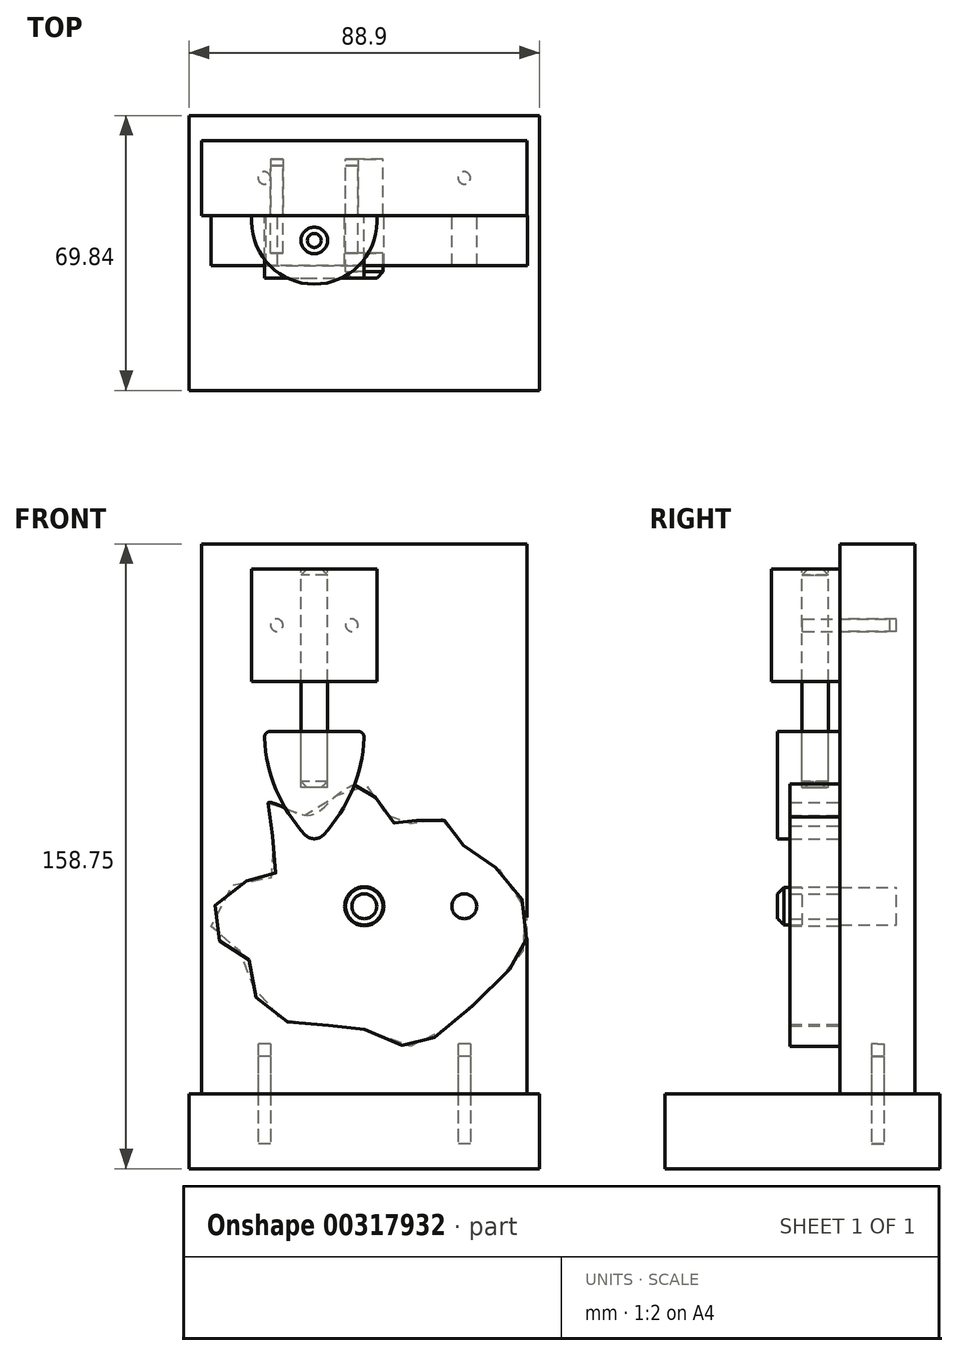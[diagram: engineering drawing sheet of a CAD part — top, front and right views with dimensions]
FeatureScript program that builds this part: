
annotation { "Feature Type Name" : "Feature", "Feature Type Description" : "" }
export const myFeature = defineFeature(function(context is Context, id is Id, definition is map)
    precondition{}
    {
        {
            var Q0;
            Q0=qCreatedBy(makeId("Top.planeOp"),FACE);
            var sketch = newSketch(context, id + "F0", { "sketchPlane" : qUnion([Q0])});
            skLineSegment(sketch, "E0.bottom", {"start": v(44.45, 34.93) * mm, "end": v(-44.45, 34.93) * mm});
            skLineSegment(sketch, "E0.top", {"start": v(44.45, -34.93) * mm, "end": v(-44.45, -34.93) * mm});
            skLineSegment(sketch, "E0.left", {"start": v(44.45, 34.92) * mm, "end": v(44.45, -34.93) * mm});
            skLineSegment(sketch, "E0.right", {"start": v(-44.45, 34.93) * mm, "end": v(-44.45, -34.93) * mm});
            skPoint(sketch, "E0.middle", {"position": v(0, 0) * mm});
            skSolve(sketch);
        }
        {
            var Q0;
            Q0=qCreatedBy(makeId("Front.planeOp"),FACE);
            cPlane(context, id + "F1", {"entities" : qUnion([Q0]), "cplaneType" : CPlaneType.OFFSET, "offset" : 28.57 * mm, "oppositeDirection" : true, "width" : 152.4 * mm, "height" : 152.4 * mm});
        }
        {
            var Q0;
            Q0=qCreatedBy(id+"F1.planeOp",FACE);
            var sketch = newSketch(context, id + "F2", { "sketchPlane" : qUnion([Q0])});
            skLineSegment(sketch, "E1.bottom", {"start": v(41.28, 0) * mm, "end": v(-41.28, 0) * mm});
            skLineSegment(sketch, "E1.top", {"start": v(41.27, 139.7) * mm, "end": v(-41.27, 139.7) * mm});
            skLineSegment(sketch, "E1.left", {"start": v(41.28, 0) * mm, "end": v(41.28, 139.7) * mm});
            skLineSegment(sketch, "E1.right", {"start": v(-41.28, 0) * mm, "end": v(-41.27, 139.7) * mm});
            skLineSegment(sketch, "E2", {"start": v(0, 0) * mm, "end": v(0, 139.7) * mm, "construction": true});
            skSolve(sketch);
        }
        {
            var Q0;
            Q0=makeQuery(id+"F0.imprint","IMPRINT",FACE,{"disambiguationData":[TD([[makeQuery(id+"F0.imprint","IMPRINT",EDGE,{"derivedFrom":sQuery(id+"F0.wireOp",EDGE,"E0.bottom")}),1.0]])]});
            extrude(context, id + "F3", {"entities" : qUnion([Q0]), "oppositeDirection" : true, "depth" : 19.05 * mm});
        }
        {
            var Q0;
            Q0=makeQuery(id+"F2.imprint","IMPRINT",FACE,{"disambiguationData":[TD([[makeQuery(id+"F2.imprint","IMPRINT",EDGE,{"derivedFrom":sQuery(id+"F2.wireOp",EDGE,"E1.bottom")}),-1.0]])]});
            extrude(context, id + "F4", {"entities" : qUnion([Q0]), "depth" : 19.05 * mm});
        }
        {
            var Q0;
            Q0=qCreatedBy(makeId("Top.planeOp"),FACE);
            var sketch = newSketch(context, id + "F5", { "sketchPlane" : qUnion([Q0])});
            skPoint(sketch, "E3.0", {"position": v(-41.27, 19.05) * mm});
            skPoint(sketch, "E4.0", {"position": v(41.28, 19.05) * mm});
            skLineSegment(sketch, "E5", {"start": v(-41.27, 19.05) * mm, "end": v(41.28, 19.05) * mm, "construction": true});
            skPoint(sketch, "E6.0", {"position": v(0, 9.53) * mm});
            skPoint(sketch, "E7.0", {"position": v(0, 28.58) * mm});
            skLineSegment(sketch, "E8", {"start": v(0, 28.58) * mm, "end": v(0, 9.53) * mm, "construction": true});
            skPoint(sketch, "E9", {"position": v(-25.4, 19.05) * mm});
            skPoint(sketch, "E10", {"position": v(25.4, 19.05) * mm});
            skCircle(sketch, "E11", {"center": v(-25.4, 19.05) * mm, "radius": 1.59 * mm});
            skCircle(sketch, "E12", {"center": v(25.4, 19.05) * mm, "radius": 1.59 * mm});
            skSolve(sketch);
        }
        {
            var Q0;
            Q0 = qSketchRegion(id + "F5", true);
            var Q1;
            Q1=sQuery(id+"F5.wireOp",EDGE,"E11");
            var Q2;
            Q2=sQuery(id+"F5.wireOp",EDGE,"E12");
            extrude(context, id + "F6", {"entities" : qUnion([Q0]), "operationType" : NewBodyOperationType.REMOVE, "surfaceEntities" : qUnion([Q1, Q2]), "endBound" : BoundingType.SYMMETRIC, "depth" : 25.4 * mm});
        }
        {
            var Q0;
            Q0 = qSketchRegion(id + "F5", true);
            extrude(context, id + "F7", {"entities" : qUnion([Q0]), "depth" : 9.52 * mm, "hasSecondDirection" : true, "secondDirectionOppositeDirection" : true, "secondDirectionDepth" : 12.7 * mm});
        }
        {
            var Q0;
            Q0=makeQuery(id+"F4.opExtrude","CAP_FACE",FACE,{"disambiguationData":[OSD([sQuery(id+"F2.wireOp",EDGE,"E1.bottom"),sQuery(id+"F2.wireOp",EDGE,"E1.top"),sQuery(id+"F2.wireOp",EDGE,"E1.left"),sQuery(id+"F2.wireOp",EDGE,"E1.right")])],"isStart":false});
            var sketch = newSketch(context, id + "F8", { "sketchPlane" : qUnion([Q0])});
            skPoint(sketch, "E13", {"position": v(0, 47.63) * mm});
            skCircle(sketch, "E14", {"center": v(0, 47.63) * mm, "radius": 4.76 * mm});
            skCircle(sketch, "E15", {"center": v(-22.22, 119.03) * mm, "radius": 1.59 * mm});
            skLineSegment(sketch, "E16", {"start": v(-22.22, 119.03) * mm, "end": v(-3.17, 119.03) * mm, "construction": true});
            skCircle(sketch, "E17", {"center": v(-3.17, 119.03) * mm, "radius": 1.59 * mm});
            skSolve(sketch);
        }
        {
            var Q0;
            Q0 = qSketchRegion(id + "F8", true);
            extrude(context, id + "F9", {"entities" : qUnion([Q0]), "operationType" : NewBodyOperationType.REMOVE, "oppositeDirection" : true, "depth" : 14.29 * mm});
        }
        {
            var Q0;
            Q0=makeQuery(id+"F8.imprint","IMPRINT",FACE,{"disambiguationData":[TD([[makeQuery(id+"F8.imprint","IMPRINT",EDGE,{"derivedFrom":sQuery(id+"F8.wireOp",EDGE,"E14")}),1.0]])]});
            extrude(context, id + "F10", {"entities" : qUnion([Q0]), "depth" : 15.88 * mm, "hasSecondDirection" : true, "secondDirectionOppositeDirection" : true, "secondDirectionDepth" : 14.29 * mm});
        }
        {
            var Q0;
            Q0=makeQuery(id+"F10.opExtrude","CAP_EDGE",EDGE,{"disambiguationData":[OSD([sQuery(id+"F8.wireOp",EDGE,"E14")])],"isStart":false});
            chamfer(context, id + "F11", {"entities" : qUnion([Q0]), "width" : 1.59 * mm, "tangentPropagation" : true});
        }
        {
            var Q0;
            Q0=makeQuery(id+"F4.opExtrude","SWEPT_FACE",FACE,{"disambiguationData":[OSD([sQuery(id+"F2.wireOp",EDGE,"E1.top")])]});
            cPlane(context, id + "F12", {"entities" : qUnion([Q0]), "cplaneType" : CPlaneType.OFFSET, "offset" : 6.35 * mm, "oppositeDirection" : true, "width" : 152.4 * mm, "height" : 152.4 * mm});
        }
        {
            var Q0;
            Q0=qCreatedBy(id+"F12.planeOp",FACE);
            var sketch = newSketch(context, id + "F13", { "sketchPlane" : qUnion([Q0])});
            skPoint(sketch, "E18.0", {"position": v(-12.7, 9.53) * mm});
            skPoint(sketch, "E19", {"position": v(-12.7, 7.94) * mm});
            skCircle(sketch, "E20", {"center": v(-12.7, 3.18) * mm, "radius": 3.37 * mm});
            skLineSegment(sketch, "E21", {"start": v(-12.7, 9.53) * mm, "end": v(-12.7, 3.18) * mm, "construction": true});
            skArc(sketch, "E22", {"start": v(-28.57, 7.94) * mm, "mid": v(-12.7, -7.94) * mm, "end": v(3.18, 7.94) * mm});
            skLineSegment(sketch, "E23", {"start": v(-28.57, 7.94) * mm, "end": v(-28.57, 9.53) * mm});
            skLineSegment(sketch, "E24", {"start": v(-28.57, 9.53) * mm, "end": v(3.18, 9.53) * mm});
            skLineSegment(sketch, "E25", {"start": v(3.18, 9.53) * mm, "end": v(3.18, 7.94) * mm});
            skSolve(sketch);
        }
        {
            var Q0;
            Q0=makeQuery(id+"F13.imprint","IMPRINT",FACE,{"disambiguationData":[TD([[makeQuery(id+"F13.imprint","IMPRINT",EDGE,{"derivedFrom":sQuery(id+"F13.wireOp",EDGE,"E20")}),-1.0]])]});
            extrude(context, id + "F14", {"entities" : qUnion([Q0]), "oppositeDirection" : true, "depth" : 28.57 * mm});
        }
        {
            var Q0;
            Q0=sQuery(id+"F8.wireOp",EDGE,"E17");
            var Q1;
            Q1=sQuery(id+"F8.wireOp",EDGE,"E15");
            extrude(context, id + "F15", {"bodyType" : ToolBodyType.SURFACE, "surfaceEntities" : qUnion([Q0, Q1]), "depth" : 1.59 * mm});
        }
        {
            var Q0;
            Q0=makeQuery(id+"F13.imprint","IMPRINT",FACE,{"disambiguationData":[TD([[makeQuery(id+"F13.imprint","IMPRINT",EDGE,{"derivedFrom":sQuery(id+"F13.wireOp",EDGE,"E20")}),1.0]])]});
            extrude(context, id + "F16", {"entities" : qUnion([Q0]), "oppositeDirection" : true, "depth" : 55.56 * mm});
        }
        {
            var Q0;
            Q0=makeQuery(id+"F8.imprint","IMPRINT",FACE,{"disambiguationData":[TD([[makeQuery(id+"F8.imprint","IMPRINT",EDGE,{"derivedFrom":sQuery(id+"F8.wireOp",EDGE,"E14")}),-1.0]])]});
            var sketch = newSketch(context, id + "F17", { "sketchPlane" : qUnion([Q0])});
            skLineSegment(sketch, "E26", {"start": v(-23.78, 92.08) * mm, "end": v(-1.62, 92.08) * mm});
            skLineSegment(sketch, "E27", {"start": v(-12.7, 92.08) * mm, "end": v(-12.7, 63.5) * mm, "construction": true});
            skArc(sketch, "E28", {"start": v(-10.38, 65.78) * mm, "mid": v(-3, 77.17) * mm, "end": v(-0.04, 90.42) * mm});
            skArc(sketch, "E29.MirrorCS", {"start": v(-15.02, 65.78) * mm, "mid": v(-22.4, 77.17) * mm, "end": v(-25.36, 90.42) * mm});
            skPoint(sketch, "E30.visualSharp", {"position": v(-25.4, 92.08) * mm});
            skArc(sketch, "E30.filletArc", {"start": v(-23.78, 92.08) * mm, "mid": v(-24.92, 91.59) * mm, "end": v(-25.36, 90.42) * mm});
            skPoint(sketch, "E31.visualSharp", {"position": v(0, 92.08) * mm});
            skArc(sketch, "E31.filletArc", {"start": v(-0.04, 90.42) * mm, "mid": v(-0.48, 91.59) * mm, "end": v(-1.62, 92.08) * mm});
            skPoint(sketch, "E32.visualSharp", {"position": v(-12.7, 63.5) * mm});
            skArc(sketch, "E32.filletArc", {"start": v(-15.02, 65.78) * mm, "mid": v(-12.7, 64.77) * mm, "end": v(-10.38, 65.78) * mm});
            skSolve(sketch);
        }
        {
            var Q0;
            Q0 = qSketchRegion(id + "F17", true);
            extrude(context, id + "F18", {"entities" : qUnion([Q0]), "depth" : 15.88 * mm});
        }
        {
            var Q0;
            Q0=makeQuery(id+"F18.opExtrude","SWEPT_BODY",BODY,{"disambiguationData":[OSD([sQuery(id+"F17.wireOp",EDGE,"E26"),sQuery(id+"F17.wireOp",EDGE,"E28"),sQuery(id+"F17.wireOp",EDGE,"E29.MirrorCS"),sQuery(id+"F17.wireOp",EDGE,"E30.filletArc"),sQuery(id+"F17.wireOp",EDGE,"E31.filletArc"),sQuery(id+"F17.wireOp",EDGE,"E32.filletArc")])]});
            var Q1;
            Q1=makeQuery(id+"F16.opExtrude","SWEPT_BODY",BODY,{"disambiguationData":[OSD([sQuery(id+"F13.wireOp",EDGE,"E20")])]});
            booleanBodies(context, id + "F19", {"operationType" : BooleanOperationType.INTERSECTION, "tools" : qUnion([Q0, Q1]), "keepTools" : true});
        }
        {
            var Q0;
            Q0=makeQuery(id+"F16.opExtrude","CAP_EDGE",EDGE,{"disambiguationData":[OSD([sQuery(id+"F13.wireOp",EDGE,"E20")])],"isStart":false});
            var Q1;
            Q1=makeQuery(id+"F16.opExtrude","CAP_EDGE",EDGE,{"disambiguationData":[OSD([sQuery(id+"F13.wireOp",EDGE,"E20")])],"isStart":true});
            chamfer(context, id + "F20", {"entities" : qUnion([Q0, Q1]), "width" : 1.59 * mm, "tangentPropagation" : true});
        }
        {
            var Q0;
            Q0=makeQuery(id+"F8.imprint","IMPRINT",FACE,{"disambiguationData":[TD([[makeQuery(id+"F8.imprint","IMPRINT",EDGE,{"derivedFrom":sQuery(id+"F8.wireOp",EDGE,"E14")}),-1.0]])]});
            var sketch = newSketch(context, id + "F21", { "sketchPlane" : qUnion([Q0])});
            skPoint(sketch, "E33.0", {"position": v(0, 47.63) * mm});
            skCircle(sketch, "E34", {"center": v(0, 47.63) * mm, "radius": 4.96 * mm});
            skCircle(sketch, "E35", {"center": v(25.4, 47.63) * mm, "radius": 3.18 * mm});
            skLineSegment(sketch, "E36", {"start": v(0, 47.63) * mm, "end": v(25.4, 47.63) * mm, "construction": true});
            skFitSpline(sketch, "E37", {"points": [v(-24.47, 73.9) * mm, v(-14.78, 70.74) * mm, v(-7.03, 75.83) * mm, v(0, 78.5) * mm, v(4.36, 72.68) * mm, v(9.2, 68.08) * mm, v(14.05, 69.77) * mm, v(20.6, 69.29) * mm, v(25.92, 62.26) * mm, v(37.07, 54.51) * mm, v(41.43, 40.7) * mm, v(36.83, 31.5) * mm, v(20.1, 15.99) * mm, v(10.42, 12.11) * mm, v(-2.42, 17.2) * mm, v(-13.8, 17.2) * mm, v(-26.9, 23.26) * mm, v(-29.8, 34.64) * mm, v(-38.28, 40.46) * mm, v(-33.92, 52.81) * mm, v(-23.5, 55) * mm, v(-22.77, 63.23) * mm, v(-24.47, 73.9) * mm]});
            skSolve(sketch);
        }
        {
            var Q0;
            Q0 = qSketchRegion(id + "F21", true);
            extrude(context, id + "F22", {"entities" : qUnion([Q0]), "depth" : 12.7 * mm});
        }
        {
            var Q0;
            Q0 = qSketchRegion(id + "F8", true);
            extrude(context, id + "F23", {"entities" : qUnion([Q0]), "operationType" : NewBodyOperationType.REMOVE, "depth" : 9.52 * mm});
        }
        {
            var Q0;
            Q0=makeQuery(id+"F8.imprint","IMPRINT",FACE,{"disambiguationData":[TD([[makeQuery(id+"F8.imprint","IMPRINT",EDGE,{"derivedFrom":sQuery(id+"F8.wireOp",EDGE,"E17")}),1.0]])]});
            var Q1;
            Q1=makeQuery(id+"F8.imprint","IMPRINT",FACE,{"disambiguationData":[TD([[makeQuery(id+"F8.imprint","IMPRINT",EDGE,{"derivedFrom":sQuery(id+"F8.wireOp",EDGE,"E15")}),1.0]])]});
            var Q2;
            Q2=sQuery(id+"F8.wireOp",EDGE,"E17");
            var Q3;
            Q3=sQuery(id+"F8.wireOp",EDGE,"E15");
            extrude(context, id + "F24", {"entities" : qUnion([Q0, Q1]), "surfaceEntities" : qUnion([Q2, Q3]), "depth" : 9.52 * mm, "hasSecondDirection" : true, "secondDirectionOppositeDirection" : true, "secondDirectionDepth" : 12.7 * mm});
        }
    });
